# Revit family: Hydrablock C 12 14 16 T
name_source: partatom
category: Attrezzatura meccanica
units: mm (PartAtom-declared; Revit-internal decimal feet)

## family parameters
Basato su piano di lavoro = No
Condiviso = No
Mantieni orientamento annotazione = No
Numero OmniClass = 23.75.00.00
Punto di calcolo locali = No
Quota connettore circolare = Usa diametro
Sempre verticale = Sì
Taglio con vuoti quando caricato = No
Tipo di parte = Normale
Titolo OmniClass = Climate Control (HVAC)

## types (3) — shared parameters
Air Flow = 5200.00 m³/h
Casing color = SB2403
Compressor = 1
Condensation = air
Depth = 410 mm  [stored 1.34514 ft]
Descrizione = Heat pump
Gas = R32
Height = 865 mm  [stored 2.83793 ft]
Installation = Outdoor installation
MOP (Maximum overcurrent protection) = 3 A
Min cable selection (power wiring) = 2.5 mm2
Net Weight = 120.00 kg
Power supply = 380-415V 3N~50Hz
Produttore = Midea
Series = M thermal Power
M thermal Power
M thermal Power
URL = https://mbt.midea.com
Water piping connections = 31.75 mm
Width = 1040 mm  [stored 3.41207 ft]
clearance access behind = 300 mm  [stored 0.984252 ft]
clearance access front = 1500 mm  [stored 4.92126 ft]
clearance access left = 500 mm  [stored 1.64042 ft]
clearance access right = 500 mm  [stored 1.64042 ft]
zero-valued in all types: Prospetto di default

## per-type parameters (varying)
| type | Cooling Power Input (EWT 23⁰C, LWT 18⁰C) | Cooling Power Input(EWT 12⁰C, LWT 7⁰C) | Cooling capacity (EWT 12⁰C, LWT 7⁰C) | Cooling capacity (EWT 23⁰C, LWT 18⁰C) | Heating Power Input (EWT 30⁰C, LWT 35⁰C) | Heating Power Input (EWT 40⁰C, LWT 45⁰C) | Heating capacity (EWT 30⁰C, LWT 35⁰C) | Heating capacity (EWT 40⁰C, LWT 45⁰C) | Minimum Circuit Amps | Modello |
| Hydrablock C 12 T | 2.65 kW | 3.74 kW | 11.60 kW | 12.20 kW | 2.49 kW | 3.38 kW | 12.20 kW | 12.50 kW | 10 A | MHC-V12WD2RN8-C |
| Hydrablock C 14 T | 3.16 kW | 4.57 kW | 13.40 kW | 13.90 kW | 3.00 kW | 4.09 kW | 14.10 kW | 14.50 kW | 11 A | MHC-V14WD2RN8-C |
| Hydrablock C 16 T | 3.67 kW | 4.83 kW | 14.00 kW | 15.40 kW | 3.56 kW | 4.70 kW | 16.00 kW | 16.20 kW | 12 A | MHC-V16WD2RN8-C |

note: [stored X ft] marks values corroborated as IEEE doubles in the binary element streams (Revit-internal decimal feet)

## geometry (parser evidence)
native form markers: Blend x3, Sweep x30
no freeform markers — native parametric forms only
